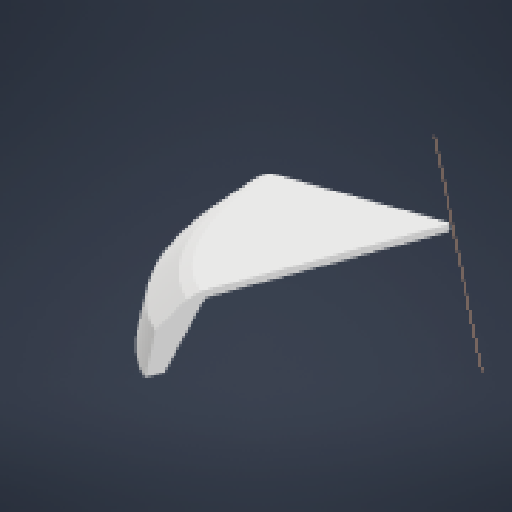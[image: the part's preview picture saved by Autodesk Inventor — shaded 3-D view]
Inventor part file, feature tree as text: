
AUTODESK INVENTOR PART (.ipt)
format: ipt  version: 2024 (Build 280153000, 153)  size: 121,856 bytes
history: native  units: in
note: dims shown in document units (in); Inventor stores cm internally (conversion verified against a paired STEP export)
features: other x4, reference x2, sketch x1, revolve x1
ambient origin geometry x8: Origin, YZ Plane, XZ Plane, XY Plane, X Axis, Y Axis, Z Axis, Center Point
bodies: Solid1 (feature_tree)
feature tree (8):
  sketch  "Sketch1"  dims[d0=60.0deg]
  other  "Work Axis1"
  revolve  "Revolution1"  [1 undecoded]
  reference  "Reference1"
  reference  "Reference2"
  other  "<userpath>\Desktop\SeniorDesign\Head_Assembly.iam"
  other  "Head_Assembly.iam"
  other  "Head_CameraPanel_Bottom:1"
note: 1 required parameter value undecoded (feature->parameter linkage not recoverable at this tier; creation-order binding heuristic only, values carry confidence <= 0.55)
